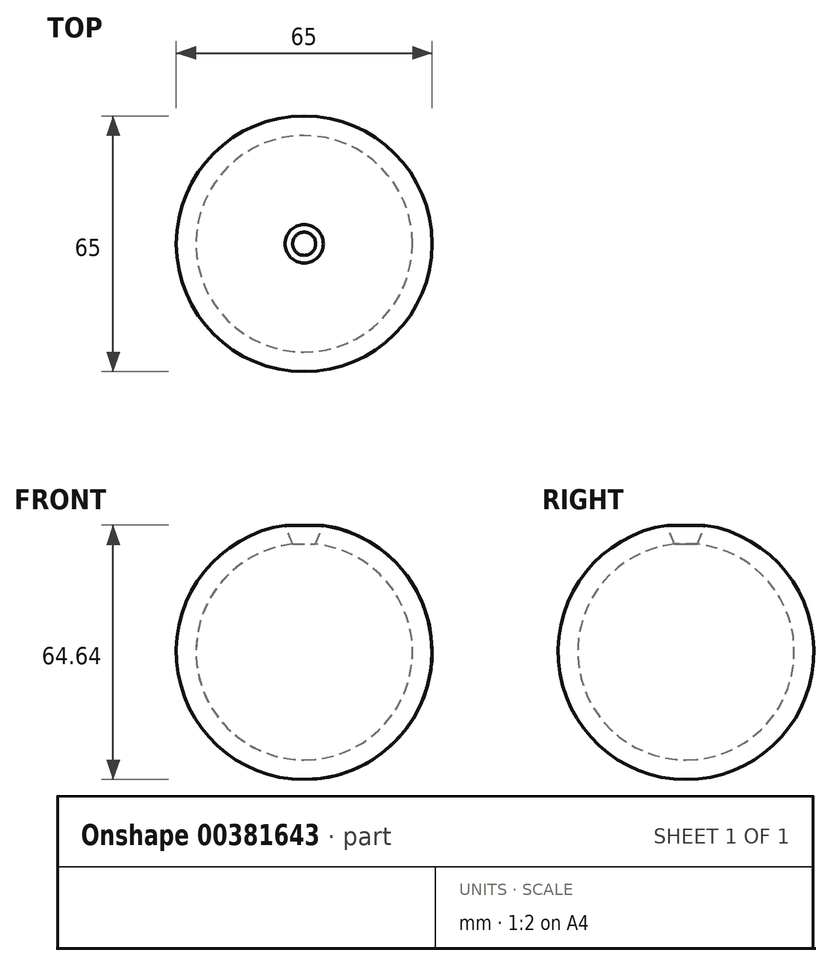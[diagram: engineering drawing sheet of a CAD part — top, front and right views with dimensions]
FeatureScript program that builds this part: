
annotation { "Feature Type Name" : "Feature", "Feature Type Description" : "" }
export const myFeature = defineFeature(function(context is Context, id is Id, definition is map)
    precondition{}
    {
        {
            var Q0;
            Q0=qCreatedBy(makeId("Front.planeOp"),FACE);
            var sketch = newSketch(context, id + "F0", { "sketchPlane" : qUnion([Q0])});
            skLineSegment(sketch, "E0", {"start": v(0, -32.5) * mm, "end": v(0, 32.5) * mm});
            skArc(sketch, "E1", {"start": v(0, 32.5) * mm, "mid": v(-32.5, 0) * mm, "end": v(0, -32.5) * mm});
            skArc(sketch, "E2", {"start": v(0, 27.5) * mm, "mid": v(-27.5, 0) * mm, "end": v(0, -27.5) * mm});
            skSolve(sketch);
        }
        {
            var Q0;
            {var subQ0=sQuery(id+"F0.wireOp",EDGE,"E1");Q0=makeQuery(id+"F0.imprint","IMPRINT",FACE,{"disambiguationData":[TD([[makeQuery(id+"F0.imprint","IMPRINT",EDGE,{"derivedFrom":subQ0}),1.0]])]});}
            var Q1;
            Q1=sQuery(id+"F0.wireOp",EDGE,"E0");
            revolve(context, id + "F1", {"entities" : qUnion([Q0]), "axis" : qUnion([Q1]), "revolveType" : RevolveType.FULL});
        }
        {
            var Q0;
            Q0=qCreatedBy(makeId("Front.planeOp"),FACE);
            var sketch = newSketch(context, id + "F2", { "sketchPlane" : qUnion([Q0])});
            skLineSegment(sketch, "E3", {"start": v(0, 20) * mm, "end": v(6, 35) * mm});
            skLineSegment(sketch, "E4", {"start": v(6, 35) * mm, "end": v(-6, 35) * mm});
            skLineSegment(sketch, "E5", {"start": v(-6, 35) * mm, "end": v(0, 20) * mm});
            skLineSegment(sketch, "E6", {"start": v(0, 35) * mm, "end": v(0, 20) * mm});
            skSolve(sketch);
        }
        {
            var Q0;
            {var subQ0=sQuery(id+"F2.wireOp",EDGE,"E5");Q0=makeQuery(id+"F2.imprint","IMPRINT",FACE,{"disambiguationData":[TD([[makeQuery(id+"F2.imprint","IMPRINT",EDGE,{"derivedFrom":subQ0}),1.0]])]});}
            var Q1;
            Q1=sQuery(id+"F2.wireOp",EDGE,"E6");
            revolve(context, id + "F3", {"operationType" : NewBodyOperationType.REMOVE, "entities" : qUnion([Q0]), "axis" : qUnion([Q1]), "revolveType" : RevolveType.FULL, "oppositeDirection" : true});
        }
    });
